# Revit family: VRIG-4104
name_source: partatom
category: Lighting Fixtures
units: mm (PartAtom-declared; Revit-internal decimal feet)

## family parameters
Always vertical = Yes
Cut with Voids When Loaded = No
Host = Ceiling
Light Source = Yes
OmniClass Number = 23.80.70.11.14.17
OmniClass Title = Direct/Indirect
Part Type = Normal
Room Calculation Point = No
Round Connector Dimension = Use Diameter
Shared = No

## types (4) — shared parameters
Color Filter = 16777215
Description = LED Vandal Resistant Recessed Grid (T-Bar) Inset Door
Dimming Lamp Color Temperature Shift = <None>
Emit Shape Visible in Rendering = No
Emit from Rectangle Width = 1' - 11 3/4"
Flat Lens Finish = Acrylic - Viscor - Clear Lens
Housing Finish = Metal - Viscor - White
Inner Diffuser Finish = Acrylic - Viscor - Frosted Prismatic P12
Lamp = LED
Manufacturer = Certolux By Viscor
Model = VRIG-4104
Tilt Angle = 90.00°
URL = https://www.viscor.com
Voltage = 120 V
Width = 1' - 11 3/4"

## per-type parameters (varying)
| type | Apparent Load | Emit from Rectangle Length | Lamp Wattage | Length | Photometric Web File |
| VRIG-4104-2X2-LED840K033LUNV | 33 VA | 1' - 11 3/4" | 33 VA | 1' - 11 3/4" | VRIG-4104-2X2-LED840K033LUNV.ies |
| VRIG-4104-2X4-LED840K039LUNV | 40 VA | 3' - 11 3/4" | 40 VA | 3' - 11 3/4" | VRIG-4104-2X4-LED840K039LUNV.ies |
| VRIG-4104-2X4-LED840K052LUNV | 46 VA | 3' - 11 3/4" | 46 VA | 3' - 11 3/4" | VRIG-4104-2X4-LED840K052LUNV.ies |
| VRIG-4104-2X4-LED840K078LUNV | 67 VA | 3' - 11 3/4" | 67 VA | 3' - 11 3/4" | VRIG-4104-2X4-LED840K078LUNV.ies |

## geometry (parser evidence)
native form markers: Sweep x3
no freeform markers — native parametric forms only
